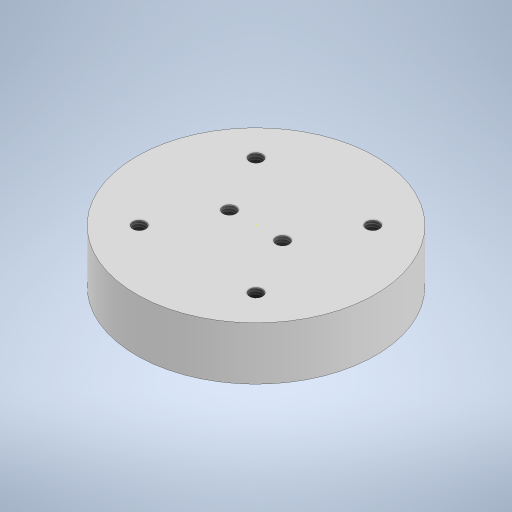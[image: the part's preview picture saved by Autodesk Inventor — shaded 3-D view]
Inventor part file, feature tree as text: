
AUTODESK INVENTOR PART (.ipt)
format: ipt  version: 2023 (Build 270158000, 158)  size: 236,032 bytes
history: native  units: mm
features: sketch x4, hole x2, other x1, extrude x1
ambient origin geometry x8: Origin, YZ Plane, XZ Plane, XY Plane, X Axis, Y Axis, Z Axis, Center Point
bodies: Body1 (feature_tree)
feature tree (8):
  other  "Твердое тело1"
  extrude  "Выдавливание1"  Depth=45.0mm
  hole  "Отверстие1"  [1 undecoded]
  sketch  "Эскиз3"
  hole  "Отверстие2"  [1 undecoded]
  sketch  "Эскиз1"
  sketch  "Эскиз2"
  sketch  "Эскиз4"
note: 2 required parameter values undecoded (feature->parameter linkage not recoverable at this tier; creation-order binding heuristic only, values carry confidence <= 0.55)
